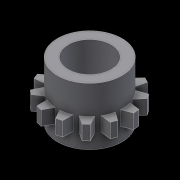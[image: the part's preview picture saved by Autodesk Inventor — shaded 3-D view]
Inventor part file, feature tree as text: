
AUTODESK INVENTOR PART (.ipt)
format: ipt  version: 2015 (Build 190159000, 159)  size: 150,528 bytes
history: native  units: mm
features: extrude x4, sketch x4, projected_geometry x2, other x1, pattern_circular x1, boolean_combine x1
ambient origin geometry x8: Origin, YZ Plane, XZ Plane, XY Plane, X Axis, Y Axis, Z Axis, Center Point
bodies: Solid1 (feature_tree), Solid2 (feature_tree)
feature tree (13):
  other  "ChainGear"
  extrude  "Extrusion1"  Depth=3.0mm
  extrude  "Extrusion3"  Depth=1.0mm
  extrude  "Extrusion2"  Depth=19.024089mm
  extrude  "Extrusion4"  Depth=4.0mm TaperAngle=360.0deg
  pattern_circular  "Circular Pattern1"  [2 undecoded]
  boolean_combine  "Combine1"
  sketch  "Sketch1"  dims[d0=6.0mm d1=3.0mm]
  sketch  "Sketch2"  dims[d2=1.0mm d3=0.0mm d4=1.0mm]
  sketch  "Sketch3"  dims[d5=0.3mm d8=19.024089mm]
  projected_geometry  "Projected Loop1"
  sketch  "Sketch4"  dims[d9=1.0mm d10=0.0mm d11=90.0mm d12=360.0deg d14=1.0mm d15=0.0mm d16=4.0mm d17=0.0mm]
  projected_geometry  "Projected Loop2"
note: 2 required parameter values undecoded (feature->parameter linkage not recoverable at this tier; creation-order binding heuristic only, values carry confidence <= 0.55)
